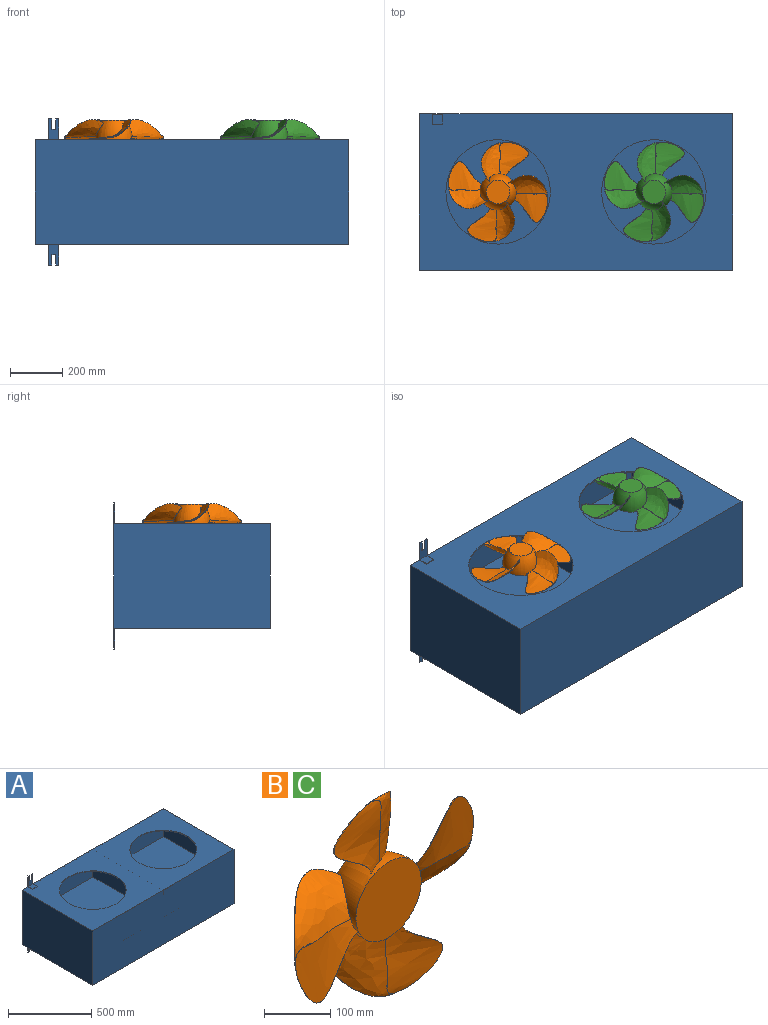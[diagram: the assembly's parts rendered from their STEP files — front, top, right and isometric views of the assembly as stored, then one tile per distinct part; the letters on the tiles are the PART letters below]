
ASSEMBLY  parts=3 mates=1
PART A: 40 faces, bbox 1200x600x560 mm
  f0: cylinder r=200mm len=400mm, axis (0,0,1), area 6283.2mm2, adj f13,f19
  f1: cylinder r=200mm len=400mm, axis (0,0,1), area 6283.2mm2, adj f7,f13
  f2: plane 592.5x590mm, normal (0,0,1), area 349575mm2, adj f3,f4,f5,f6
  f3: plane 590x195mm, normal (-1,0,0), area 115050mm2, adj f2,f4,f6,f7
  f4: plane 592.5x195mm, normal (0,1,0), area 115537.5mm2, adj f2,f3,f5,f7
  f5: plane 590x195mm, normal (1,0,0), area 115050mm2, adj f2,f4,f6,f7
  f6: plane 592.5x195mm, normal (0,-1,0), area 115537.5mm2, adj f2,f3,f5,f7
  f7: plane 592.5x590mm, normal (0,0,-1), area 223911.3mm2, adj f1,f3,f4,f5,f6
  f8: plane 600x400mm, normal (1,0,0), area 240000mm2, adj f9,f11,f12,f13
  f9: plane 1200x560mm, normal (0,1,0), area 485200mm2, adj f8,f10,f12,f13,f20,f23,f25,f26
  f10: plane 600x400mm, normal (-1,0,0), area 240000mm2, adj f9,f11,f12,f13
  f11: plane 1200x400mm, normal (0,-1,0), area 480000mm2, adj f8,f10,f12,f13
  f12: plane 1200x600mm, normal (0,0,-1), area 718400mm2, adj f8,f9,f10,f11,f22,f25,f26
  f13: plane 1200x600mm, normal (0,0,1), area 467072.6mm2, adj f0,f1,f8,f9,f10,f11,f31,f35
  f14: plane 592.5x590mm, normal (0,0,1), area 349575mm2, adj f15,f16,f17,f18
  f15: plane 592.5x195mm, normal (0,-1,0), area 115537.5mm2, adj f14,f16,f18,f19
  f16: plane 590x195mm, normal (-1,0,0), area 115050mm2, adj f14,f15,f17,f19
  f17: plane 592.5x195mm, normal (0,1,0), area 115537.5mm2, adj f14,f16,f18,f19
  f18: plane 590x195mm, normal (1,0,0), area 115050mm2, adj f14,f15,f17,f19
  f19: plane 592.5x590mm, normal (0,0,-1), area 223911.3mm2, adj f0,f15,f16,f17,f18
  f20: plane 12.5x3mm, normal (0,0,-1), area 37.5mm2, adj f9,f24,f25,f27
  f21: plane 40x37mm, normal (0,0,-1), area 1480mm2, adj f22,f24,f25,f26
  f22: plane 40x3mm, normal (0,-1,0), area 120mm2, adj f12,f21,f25,f26
  f23: plane 12.5x3mm, normal (0,0,-1), area 37.5mm2, adj f9,f24,f26,f28
  f24: plane 77x40mm, normal (0,-1,0), area 2480mm2, adj f20,f21,f23,f25,f26,f27,f28,f29
  f25: plane 80x40mm, normal (1,0,0), area 351mm2, adj f9,f12,f20,f21,f22,f24
  f26: plane 80x40mm, normal (-1,0,0), area 351mm2, adj f9,f12,f21,f22,f23,f24
  f27: plane 40x3mm, normal (-1,0,0), area 120mm2, adj f9,f20,f24,f29
  f28: plane 40x3mm, normal (1,0,0), area 120mm2, adj f9,f23,f24,f29
  f29: plane 15x3mm, normal (0,0,-1), area 45mm2, adj f9,f24,f27,f28
  f30: plane 12.5x3mm, normal (0,0,1), area 37.5mm2, adj f9,f33,f35,f37
  f31: plane 40x3mm, normal (0,-1,0), area 120mm2, adj f13,f32,f35,f36
  f32: plane 40x37mm, normal (0,0,1), area 1480mm2, adj f31,f33,f35,f36
  f33: plane 77x40mm, normal (0,-1,0), area 2480mm2, adj f30,f32,f34,f35,f36,f37,f38,f39
  f34: plane 12.5x3mm, normal (0,0,1), area 37.5mm2, adj f9,f33,f36,f39
  f35: plane 80x40mm, normal (1,0,0), area 351mm2, adj f9,f13,f30,f31,f32,f33
  f36: plane 80x40mm, normal (-1,0,0), area 351mm2, adj f9,f13,f31,f32,f33,f34
  f37: plane 40x3mm, normal (-1,0,0), area 120mm2, adj f9,f30,f33,f38
  f38: plane 15x3mm, normal (0,0,1), area 45mm2, adj f9,f33,f37,f39
  f39: plane 40x3mm, normal (1,0,0), area 120mm2, adj f9,f33,f34,f38
PART B: 31 faces, bbox 381.4x78.8x381.4 mm
  f0: revolved ~139.92x139.79mm, area 6486.5mm2, adj f1,f3,f4,f5,f6,f7,f8,f10
  f1: bspline ~128.92x110.59mm, area 9361.6mm2, adj f0,f2,f3,f7
  f2: plane 9.83x1.86mm, normal (1,0,0), area 9.8mm2, adj f1,f3,f4,f5,f6,f7
  f3: bspline ~149.58x95.77mm, area 10259mm2, adj f0,f1,f2,f4
  f4: bspline ~149.89x86.95mm, area 203.2mm2, adj f0,f2,f3,f5
  f5: bspline ~149.89x86.95mm, area 10413.8mm2, adj f0,f2,f4,f6
  f6: bspline ~150.69x131mm, area 9377.4mm2, adj f0,f2,f5,f7
  f7: bspline ~127.85x85mm, area 206.1mm2, adj f0,f1,f2,f6
  f8: bspline ~128.92x110.59mm, area 9361.6mm2, adj f0,f9,f10,f14
  f9: plane 9.83x1.86mm, normal (-1,0,0), area 9.8mm2, adj f8,f10,f11,f12,f13,f14
  f10: bspline ~149.58x95.77mm, area 10259mm2, adj f0,f8,f9,f11
  f11: bspline ~149.89x86.95mm, area 203.2mm2, adj f0,f9,f10,f12
  f12: bspline ~149.89x86.95mm, area 10413.8mm2, adj f0,f9,f11,f13
  f13: bspline ~150.69x131mm, area 9377.4mm2, adj f0,f9,f12,f14
  f14: bspline ~127.85x85mm, area 206.1mm2, adj f0,f8,f9,f13
  f15: bspline ~149.89x86.95mm, area 203.2mm2, adj f0,f16,f17,f21
  f16: plane 9.83x1.86mm, normal (0,0,1), area 9.8mm2, adj f15,f17,f18,f19,f20,f21
  f17: bspline ~149.58x95.77mm, area 10269.2mm2, adj f0,f15,f16,f18
  f18: bspline ~128.92x110.59mm, area 9361.6mm2, adj f0,f16,f17,f19
  f19: bspline ~127.85x85mm, area 206.1mm2, adj f0,f16,f18,f20
  f20: bspline ~150.69x131mm, area 9377.4mm2, adj f0,f16,f19,f21
  f21: bspline ~149.89x86.95mm, area 10399.5mm2, adj f0,f15,f16,f20
  f22: bspline ~149.89x86.95mm, area 203.2mm2, adj f0,f23,f25,f29
  f23: plane 9.83x1.86mm, normal (0,0,-1), area 9.8mm2, adj f22,f25,f26,f27,f28,f29
  f24: plane 90x90mm, normal (0,1,0), area 6361.7mm2, adj f0
  f25: bspline ~149.58x95.77mm, area 10269.2mm2, adj f0,f22,f23,f26
  f26: bspline ~128.92x110.59mm, area 9361.6mm2, adj f0,f23,f25,f27
  f27: bspline ~127.85x85mm, area 206.1mm2, adj f0,f23,f26,f28
  f28: bspline ~150.69x131mm, area 9377.4mm2, adj f0,f23,f27,f29
  f29: bspline ~149.89x86.95mm, area 10399.5mm2, adj f0,f22,f23,f28
  f30: plane 140x140mm, normal (0,-1,0), area 15393.8mm2, adj f0
PART C: same geometry as B
PLACE A t=(186.12,120.71,-4.55)mm
PLACE B rot(axis=(1,0,0),90deg) t=(-112.63,120.71,395.45)mm
PLACE C rot(axis=(1,0,0),90deg) t=(484.87,120.71,395.45)mm
MATE planar A.f0 <-> B.f30  axis (0,0,1) through (-112.63,120.71,395.45)mm
